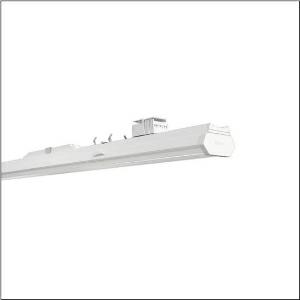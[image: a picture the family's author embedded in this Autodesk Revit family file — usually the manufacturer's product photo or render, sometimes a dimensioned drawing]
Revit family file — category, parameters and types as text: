
# Revit family: licross_r__11_protected_mo_51tp12dn595g_d325
name_source: partatom
category: Lighting Fixtures
units: mm (PartAtom-declared; Revit-internal decimal feet)

## family parameters
Cut with Voids When Loaded = No
Host = Face
Light Source = No
Part Type = Normal
Room Calculation Point = No
Round Connector Dimension = Use Diameter
Shared = No

## types (1)
- --- (1 x LED, 9820 lm, 57.1 W, 5000K)
    Apparent Load = 57 VA
    CIE Flux Codes = 73 92 98 99 100
    Color Rendering = 80
    Color Temperature = 5000K
    Default Elevation = 1800 mm
    Description = Licross® 11 Protected MO, luminaire insert, of sheet steel, galvanised, coil coated, white, length: 1.500mm, width: 90mm, height: 101mm, LED rated luminous flux: 9.820lm, light colour: 850, control gear: DALI 2, with plug, 5-pole, with phase selection, mains connection: 220..240V, AC, 50/60Hz, rated input power: 57W, internal wiring halogen-free, primary optical cover: cover, of PMMA, light emission: direct distribution, primary light characteristic: symmetric, protection rating (complete): IP64, insulation class (complete): insulation class I (protective earthing), certification: CE, ENEC, VDE, UKCA, protection symbol: D if used in an environment with conductive dust loads with corresponding accessories, impact resistance: IK06, permissible ambient temperature for indoor applications: -25..+35°C, corresponds to IFS (International Featured Standards) requirements for safety and quality in the food industry, reducing of maximum allowable ambient temperature of 5°C with ceiling mounting, LABS conformity tested according to VDMA 24364:2018-05, packaging unit: 1 piece
    Height = 92 mm
    Lamp = 1 x LED
    Lamp Light Flux = 9820 lm
    Lamp Power = 57.1 W
    Lamp count = 1
    Length = 1500 mm
    Luminous efficacy = 172 lm/W
    Manufacturer = Siteco
    ModVariant = No
    Model = 51TP12DN595G
    Mounting Place = Ceiling
    Mounting Type = Pendant
    Number of Poles = 1
    OnlyDefault = Yes
    Power Factor = 1
    Product Name = Licross® 11 Protected MO
    Product group = luminaire insert | ceiling pendant
    ProductGroupID = 902
    Protection Class = Protection class I
    Protection Degree = IP 64
    RLX_Detail_Level = 1
    RLX_Emergency_Light_Flux = 0 lm
    RLX_Emergency_Type = 0
    RLX_Emergency_Type_DB = No
    RlxData = <blob elided: 24457 chars, md5=c817dada>
    Socket = socket
    Standby Power = 0 W
    System Light Flux = 9820 lm
    System Power = 57 W
    Type Comments = factory setting: luminous flux: 100 % | dim-lin: 254 | 378 mA
    Type Image = l_1256148.jpg
    URL = http://relux.com
    VarID = @adj_042659
    Voltage = 0 V
    Weight = 0.00 kg
    Width = 88 mm

## geometry (parser evidence)
native form markers: Blend x4, Sweep x11
no freeform markers — native parametric forms only
